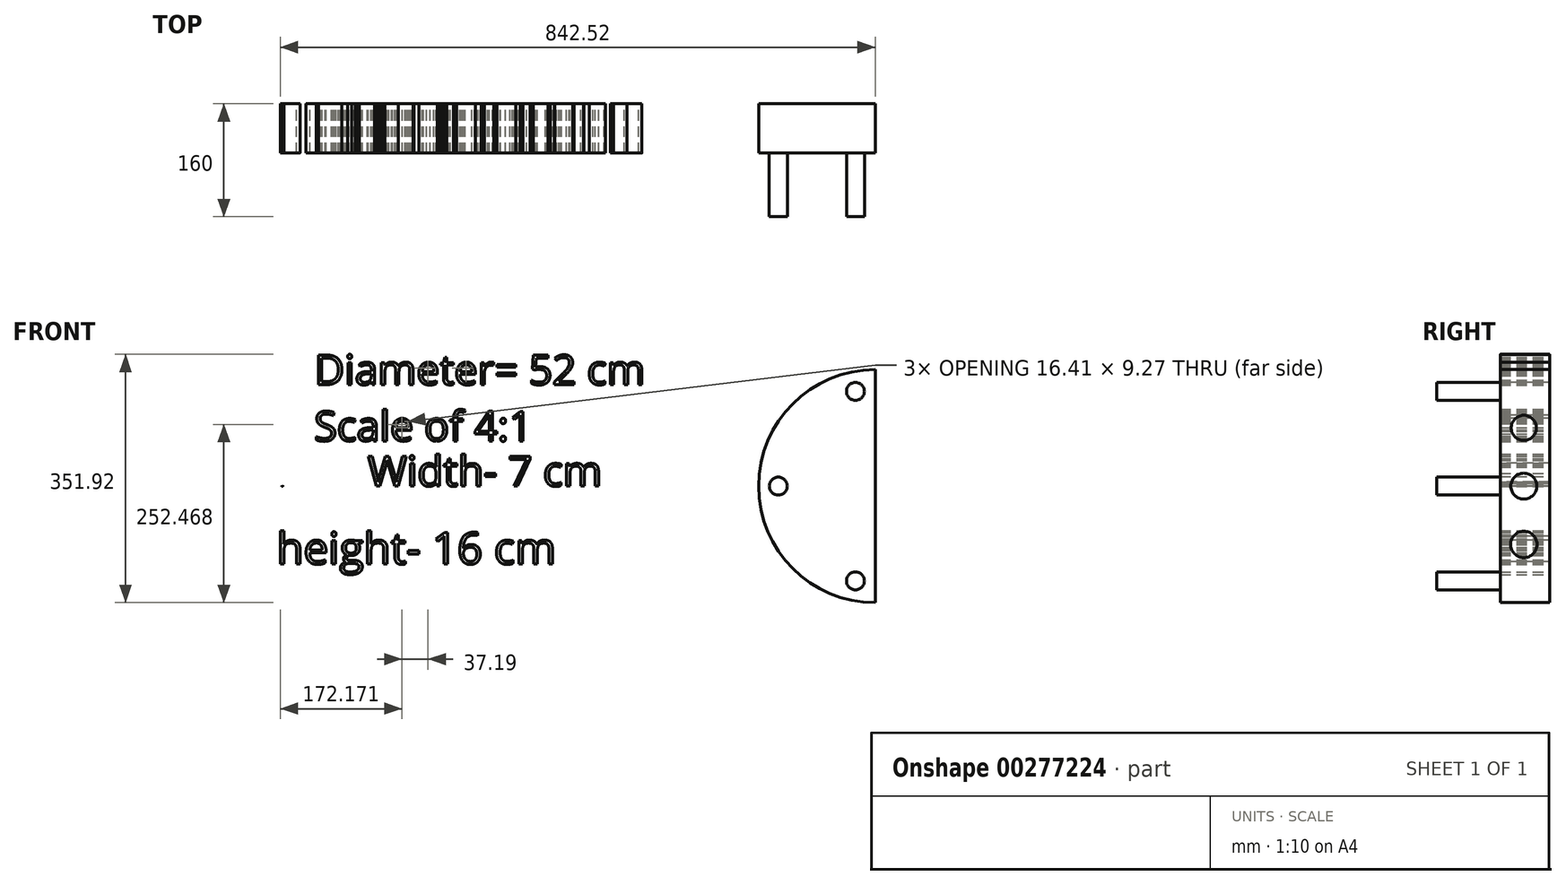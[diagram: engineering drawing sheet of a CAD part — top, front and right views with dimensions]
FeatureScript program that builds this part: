
annotation { "Feature Type Name" : "Feature", "Feature Type Description" : "" }
export const myFeature = defineFeature(function(context is Context, id is Id, definition is map)
    precondition{}
    {
        {
            var Q0;
            Q0=qCreatedBy(makeId("Front.planeOp"),FACE);
            var sketch = newSketch(context, id + "F0", { "sketchPlane" : qUnion([Q0])});
            skArc(sketch, "E0", {"start": v(0, 165.1) * mm, "mid": v(-165.1, 0) * mm, "end": v(0, -165.1) * mm});
            skText(sketch, "E1", { "text": "Diameter= 52 cm\nScale of 4:1", "fontName": "OpenSans-Regular.ttf"});
            skLineSegment(sketch, "E2", {"start": v(0, 165.1) * mm, "end": v(0, -165.1) * mm});
            skText(sketch, "E3", { "text": "Width= 6 cm", "fontName": "OpenSans-Regular.ttf"});
            skText(sketch, "E4", { "text": "Width- 7 cm", "fontName": "OpenSans-Regular.ttf"});
            skText(sketch, "E5", { "text": "height- 16 cm\n", "fontName": "OpenSans-Regular.ttf"});
            const initialGuessF0  = {"E1": [-0.7944, 0.14378, 1, 0, 0.04222], "E3": [-0.84067, -0.0003, 1, 0, 0.0003], "E4": [-0.71837, 0, 1, 0, 0.04279], "E5": [-0.84786, -0.11042, 1, 0, 0.045]};
            skSetInitialGuess(sketch, initialGuessF0);
            skSolve(sketch);
        }
        {
            var Q0;
            Q0 = qSketchRegion(id + "F0", true);
            extrude(context, id + "F1", {"entities" : qUnion([Q0]), "depth" : 70 * mm});
        }
        {
            var Q0;
            Q0=makeQuery(id+"F1.opExtrude","CAP_FACE",FACE,{"disambiguationData":[OSD([sQuery(id+"F0.wireOp",EDGE,"E0"),sQuery(id+"F0.wireOp",EDGE,"E2")])],"isStart":false});
            var sketch = newSketch(context, id + "F2", { "sketchPlane" : qUnion([Q0])});
            skCircle(sketch, "E6", {"center": v(-27.94, 134.28) * mm, "radius": 12.7 * mm});
            skCircle(sketch, "E7", {"center": v(-27.94, -134.28) * mm, "radius": 12.7 * mm});
            skCircle(sketch, "E8", {"center": v(-137.16, 0) * mm, "radius": 12.7 * mm});
            skSolve(sketch);
        }
        {
            var Q0;
            Q0 = qSketchRegion(id + "F2", true);
            extrude(context, id + "F3", {"entities" : qUnion([Q0]), "operationType" : NewBodyOperationType.ADD, "depth" : 90 * mm});
        }
        {
            var Q0;
            Q0=makeQuery(id+"F1.opExtrude","SWEPT_FACE",FACE,{"disambiguationData":[OSD([sQuery(id+"F0.wireOp",EDGE,"E2")])]});
            var sketch = newSketch(context, id + "F4", { "sketchPlane" : qUnion([Q0])});
            skLineSegment(sketch, "E9", {"start": v(-36.52, 0) * mm, "end": v(-36.52, -165.1) * mm});
            skLineSegment(sketch, "E10", {"start": v(-36.52, -165.1) * mm, "end": v(-36.52, 165.1) * mm});
            skCircle(sketch, "E11", {"center": v(-36.52, 0) * mm, "radius": 18.4 * mm});
            skCircle(sketch, "E12", {"center": v(-36.52, -82.55) * mm, "radius": 18.72 * mm});
            skCircle(sketch, "E13", {"center": v(-36.52, 82.55) * mm, "radius": 17.82 * mm});
            skSolve(sketch);
        }
        {
            var Q0;
            {var subQ0=sQuery(id+"F4.wireOp",EDGE,"E13");var subQ1=sQuery(id+"F4.wireOp",EDGE,"E10");var subQ2=makeQuery(id+"F4.imprint","INTERSECT",VERTEX,{"disambiguationData":[OD(0.0)],"derivedFrom":[subQ1,subQ0]});Q0=makeQuery(id+"F4.imprint","IMPRINT",FACE,{"disambiguationData":[TD([[makeQuery(id+"F4.imprint","IMPRINT",EDGE,{"disambiguationData":[TD([[subQ2,-1.0]])],"derivedFrom":subQ1}),-1.0]])]});}
            var Q1;
            {var subQ0=sQuery(id+"F4.wireOp",EDGE,"E13");var subQ1=sQuery(id+"F4.wireOp",EDGE,"E10");var subQ2=makeQuery(id+"F4.imprint","INTERSECT",VERTEX,{"disambiguationData":[OD(0.0)],"derivedFrom":[subQ1,subQ0]});Q1=makeQuery(id+"F4.imprint","IMPRINT",FACE,{"disambiguationData":[TD([[makeQuery(id+"F4.imprint","IMPRINT",EDGE,{"disambiguationData":[TD([[subQ2,-1.0]])],"derivedFrom":subQ1}),1.0]])]});}
            var Q2;
            {var subQ0=sQuery(id+"F4.wireOp",EDGE,"E10");var subQ1=makeQuery(id+"F4.imprint","IMPRINT",VERTEX,{"derivedFrom":subQ0});Q2=makeQuery(id+"F4.imprint","IMPRINT",FACE,{"disambiguationData":[TD([[makeQuery(id+"F4.imprint","IMPRINT",EDGE,{"disambiguationData":[TD([[subQ1,1.0]])],"derivedFrom":subQ0}),1.0]])]});}
            var Q3;
            {var subQ0=sQuery(id+"F4.wireOp",EDGE,"E10");var subQ1=makeQuery(id+"F4.imprint","IMPRINT",VERTEX,{"derivedFrom":subQ0});Q3=makeQuery(id+"F4.imprint","IMPRINT",FACE,{"disambiguationData":[TD([[makeQuery(id+"F4.imprint","IMPRINT",EDGE,{"disambiguationData":[TD([[subQ1,1.0]])],"derivedFrom":subQ0}),-1.0]])]});}
            var Q4;
            {var subQ0=sQuery(id+"F4.wireOp",EDGE,"E12");var subQ1=sQuery(id+"F4.wireOp",EDGE,"E10");var subQ2=makeQuery(id+"F4.imprint","INTERSECT",VERTEX,{"disambiguationData":[OD(0.0)],"derivedFrom":[subQ1,subQ0]});Q4=makeQuery(id+"F4.imprint","IMPRINT",FACE,{"disambiguationData":[TD([[makeQuery(id+"F4.imprint","IMPRINT",EDGE,{"disambiguationData":[TD([[subQ2,-1.0]])],"derivedFrom":subQ1}),-1.0]])]});}
            var Q5;
            {var subQ0=sQuery(id+"F4.wireOp",EDGE,"E12");var subQ1=sQuery(id+"F4.wireOp",EDGE,"E10");var subQ2=makeQuery(id+"F4.imprint","INTERSECT",VERTEX,{"disambiguationData":[OD(0.0)],"derivedFrom":[subQ1,subQ0]});Q5=makeQuery(id+"F4.imprint","IMPRINT",FACE,{"disambiguationData":[TD([[makeQuery(id+"F4.imprint","IMPRINT",EDGE,{"disambiguationData":[TD([[subQ2,-1.0]])],"derivedFrom":subQ1}),1.0]])]});}
            extrude(context, id + "F5", {"entities" : qUnion([Q0, Q1, Q2, Q3, Q4, Q5]), "operationType" : NewBodyOperationType.ADD, "depth" : 0.03 * mm});
        }
    });
